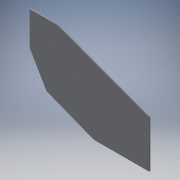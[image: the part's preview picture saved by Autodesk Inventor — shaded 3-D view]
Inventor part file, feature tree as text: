
AUTODESK INVENTOR PART (.ipt)
format: ipt  version: 2018.2 (Build 222227000, 227)  size: 135,168 bytes
history: native  units: mm
features: other x4, reference x4, extrude x3, sketch x3, chamfer x1
ambient origin geometry x8: Origin, YZ Plane, XZ Plane, XY Plane, X Axis, Y Axis, Z Axis, Center Point
bodies: Body1 (feature_tree)
feature tree (15):
  other  "ソリッド1"
  extrude  "押し出し1"  Depth=555.0mm
  extrude  "押し出し4"  Depth=555.0mm
  extrude  "押し出し5"  Depth=5.0mm TaperAngle=0.0deg
  chamfer  "面取り2"  Distance=5.0mm
  sketch  "スケッチ1"
  sketch  "スケッチ3"
  sketch  "スケッチ5"
  reference  "参照1"
  reference  "参照2"
  reference  "参照3"
  reference  "参照4"
  other  "<userpath>\Documents\Inventor\AeroCAD2018\設計\Rr.wing\model.iam"
  other  "model.iam"
  other  "endplate:1"
